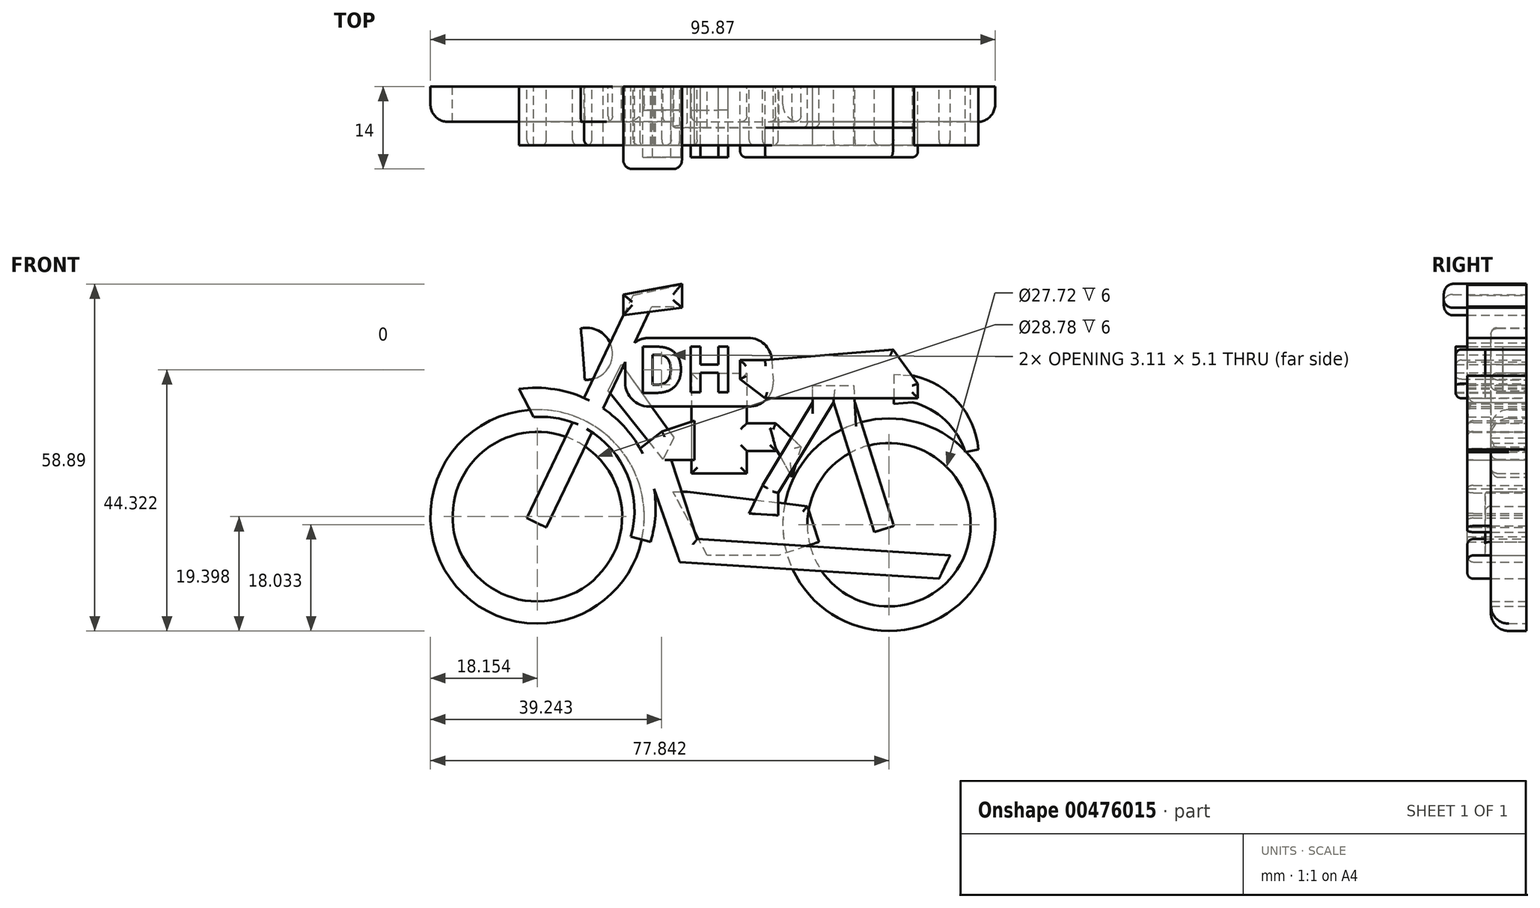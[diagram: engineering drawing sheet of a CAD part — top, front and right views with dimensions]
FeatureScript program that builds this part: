
annotation { "Feature Type Name" : "Feature", "Feature Type Description" : "" }
export const myFeature = defineFeature(function(context is Context, id is Id, definition is map)
    precondition{}
    {
        {
            var Q0;
            Q0=qCreatedBy(makeId("Front.planeOp"),FACE);
            var sketch = newSketch(context, id + "F0", { "sketchPlane" : qUnion([Q0])});
            skCircle(sketch, "E0", {"center": v(30.84, -8.07) * mm, "radius": 18.03 * mm});
            skCircle(sketch, "E1", {"center": v(30.84, -8.07) * mm, "radius": 13.86 * mm});
            skCircle(sketch, "E2", {"center": v(-28.85, -6.7) * mm, "radius": 18.15 * mm});
            skCircle(sketch, "E3", {"center": v(-28.85, -6.7) * mm, "radius": 14.4 * mm});
            skLineSegment(sketch, "E4.bottom", {"start": v(-2.69, 17.64) * mm, "end": v(6.7, 17.64) * mm});
            skLineSegment(sketch, "E4.top", {"start": v(-2.69, 0.65) * mm, "end": v(6.7, 0.65) * mm});
            skLineSegment(sketch, "E4.left", {"start": v(-2.69, 17.64) * mm, "end": v(-2.69, 0.65) * mm});
            skLineSegment(sketch, "E4.right", {"start": v(6.7, 17.64) * mm, "end": v(6.7, 0.65) * mm});
            skPoint(sketch, "E5.visualSharp", {"position": v(8.94, 22.1) * mm});
            skPoint(sketch, "E6.visualSharp", {"position": v(-12.3, 22.1) * mm});
            skPoint(sketch, "E7.visualSharp", {"position": v(-12.3, 13.62) * mm});
            skLineSegment(sketch, "E8.bottom", {"start": v(6.7, 9.14) * mm, "end": v(11.62, 9.14) * mm});
            skLineSegment(sketch, "E8.top", {"start": v(6.7, 9.14) * mm, "end": v(11.62, 9.14) * mm});
            skLineSegment(sketch, "E8.left", {"start": v(6.7, 9.14) * mm, "end": v(6.7, 9.14) * mm});
            skLineSegment(sketch, "E8.right", {"start": v(11.62, 9.14) * mm, "end": v(11.62, 9.14) * mm});
            skLineSegment(sketch, "E9.top", {"start": v(11.62, 4.45) * mm, "end": v(11.62, 4.45) * mm});
            skLineSegment(sketch, "E9.left", {"start": v(11.62, 9.14) * mm, "end": v(11.62, 4.45) * mm});
            skLineSegment(sketch, "E9.right", {"start": v(11.62, 9.14) * mm, "end": v(11.62, 4.45) * mm});
            skLineSegment(sketch, "E10.bottom", {"start": v(6.7, 4.9) * mm, "end": v(11.62, 4.9) * mm});
            skLineSegment(sketch, "E10.top", {"start": v(6.7, 4.45) * mm, "end": v(11.62, 4.45) * mm});
            skLineSegment(sketch, "E10.left", {"start": v(6.7, 4.9) * mm, "end": v(6.7, 4.45) * mm});
            skLineSegment(sketch, "E10.right", {"start": v(11.62, 4.9) * mm, "end": v(11.62, 4.45) * mm});
            skLineSegment(sketch, "E11", {"start": v(40.23, 12.05) * mm, "end": v(43.8, 15.4) * mm});
            skLineSegment(sketch, "E12", {"start": v(43.8, 15.4) * mm, "end": v(45.82, 9.14) * mm});
            skLineSegment(sketch, "E13", {"start": v(45.82, 9.14) * mm, "end": v(43.4, 8.37) * mm});
            skArc(sketch, "E14", {"start": v(-20.8, 16.52) * mm, "mid": v(-16.1, 21.27) * mm, "end": v(-21.46, 25.24) * mm});
            skLineSegment(sketch, "E15", {"start": v(-21.46, 25.24) * mm, "end": v(-20.8, 16.52) * mm});
            skLineSegment(sketch, "E16", {"start": v(11.62, 9.14) * mm, "end": v(15.89, 5.17) * mm});
            skLineSegment(sketch, "E17", {"start": v(15.89, 5.17) * mm, "end": v(14.4, 0) * mm});
            skLineSegment(sketch, "E18", {"start": v(14.4, 0) * mm, "end": v(11.62, 4.9) * mm});
            skLineSegment(sketch, "E19", {"start": v(-14.59, 19.16) * mm, "end": v(-5.65, 6.64) * mm});
            skLineSegment(sketch, "E20", {"start": v(-5.65, 6.64) * mm, "end": v(-7.52, 3.06) * mm});
            skLineSegment(sketch, "E21", {"start": v(-7.52, 3.06) * mm, "end": v(-16.82, 14.69) * mm});
            skLineSegment(sketch, "E22", {"start": v(-16.82, 14.69) * mm, "end": v(-14.59, 19.16) * mm});
            skSolve(sketch);
        }
        {
            var Q0;
            Q0=qCreatedBy(makeId("Front.planeOp"),FACE);
            var sketch = newSketch(context, id + "F1", { "sketchPlane" : qUnion([Q0])});
            skLineSegment(sketch, "E23", {"start": v(-12.62, 30.83) * mm, "end": v(-30.63, -6.95) * mm});
            skLineSegment(sketch, "E24", {"start": v(-30.63, -6.95) * mm, "end": v(-27.3, -8.54) * mm});
            skLineSegment(sketch, "E25", {"start": v(-27.3, -8.54) * mm, "end": v(-9.43, 28.94) * mm});
            skLineSegment(sketch, "E26", {"start": v(-9.43, 28.94) * mm, "end": v(-4.25, 28.94) * mm});
            skLineSegment(sketch, "E27", {"start": v(-4.25, 28.94) * mm, "end": v(-4.25, 32.61) * mm});
            skLineSegment(sketch, "E28", {"start": v(-4.25, 32.61) * mm, "end": v(-12.62, 30.83) * mm});
            skArc(sketch, "E29", {"start": v(-9.62, -10.97) * mm, "mid": v(-13.7, 8.11) * mm, "end": v(-31.97, 14.96) * mm});
            skArc(sketch, "E30", {"start": v(-12.97, -10.08) * mm, "mid": v(-15.96, 4.37) * mm, "end": v(-29.5, 10.2) * mm});
            skPoint(sketch, "E30.endSnap0", {"position": v(-18.36, 10.2) * mm});
            skLineSegment(sketch, "E31", {"start": v(-31.97, 14.96) * mm, "end": v(-29.5, 10.2) * mm});
            skLineSegment(sketch, "E32", {"start": v(-12.97, -10.08) * mm, "end": v(-9.62, -10.97) * mm});
            skArc(sketch, "E33", {"start": v(46.04, 4.67) * mm, "mid": v(42.6, 12.7) * mm, "end": v(35.09, 17.2) * mm});
            skArc(sketch, "E34", {"start": v(43.8, 4.23) * mm, "mid": v(40.43, 9.63) * mm, "end": v(34.87, 12.72) * mm});
            skLineSegment(sketch, "E35", {"start": v(35.09, 17.2) * mm, "end": v(34.87, 12.72) * mm});
            skLineSegment(sketch, "E36", {"start": v(43.8, 4.23) * mm, "end": v(46.04, 4.67) * mm});
            skLineSegment(sketch, "E37", {"start": v(25.03, 12.72) * mm, "end": v(31.64, -8.3) * mm});
            skLineSegment(sketch, "E38", {"start": v(31.64, -8.3) * mm, "end": v(28.36, -9.32) * mm});
            skLineSegment(sketch, "E39", {"start": v(28.36, -9.32) * mm, "end": v(21.42, 12.72) * mm});
            skLineSegment(sketch, "E40", {"start": v(21.42, 12.72) * mm, "end": v(25.03, 12.72) * mm});
            skLineSegment(sketch, "E41", {"start": v(17.88, 12.72) * mm, "end": v(21.42, 12.72) * mm});
            skLineSegment(sketch, "E42", {"start": v(12.07, -2.7) * mm, "end": v(9.35, -1.4) * mm});
            skLineSegment(sketch, "E43", {"start": v(9.35, -1.4) * mm, "end": v(17.88, 12.72) * mm});
            skLineSegment(sketch, "E44", {"start": v(12.07, -2.7) * mm, "end": v(21.42, 12.72) * mm});
            skLineSegment(sketch, "E45", {"start": v(-4.67, -14.4) * mm, "end": v(39.34, -17.23) * mm});
            skLineSegment(sketch, "E46", {"start": v(39.34, -17.23) * mm, "end": v(41.22, -13.28) * mm});
            skLineSegment(sketch, "E47", {"start": v(41.22, -13.28) * mm, "end": v(-1.72, -10.5) * mm});
            skLineSegment(sketch, "E48", {"start": v(-7.71, 7.77) * mm, "end": v(-2.17, 9.59) * mm});
            skLineSegment(sketch, "E49", {"start": v(-2.17, 9.59) * mm, "end": v(-2.17, 2.89) * mm});
            skLineSegment(sketch, "E50", {"start": v(-2.17, 2.89) * mm, "end": v(-6.11, 2.89) * mm});
            skLineSegment(sketch, "E51", {"start": v(9.35, -1.4) * mm, "end": v(7.08, -6.16) * mm});
            skLineSegment(sketch, "E52", {"start": v(7.08, -6.16) * mm, "end": v(9.35, -6.3) * mm});
            skLineSegment(sketch, "E53", {"start": v(9.35, -6.3) * mm, "end": v(12.07, -6.48) * mm});
            skLineSegment(sketch, "E54", {"start": v(12.07, -6.48) * mm, "end": v(12.07, -2.7) * mm});
            skLineSegment(sketch, "E55", {"start": v(35.09, 17.2) * mm, "end": v(31.64, 17.36) * mm});
            skLineSegment(sketch, "E56", {"start": v(31.64, 17.36) * mm, "end": v(31.64, 12.47) * mm});
            skLineSegment(sketch, "E57", {"start": v(31.64, 12.47) * mm, "end": v(34.87, 12.72) * mm});
            skLineSegment(sketch, "E58", {"start": v(-7.71, 7.77) * mm, "end": v(-11.42, 4.88) * mm});
            skLineSegment(sketch, "E59", {"start": v(-11.42, 4.88) * mm, "end": v(-4.67, -14.4) * mm});
            skLineSegment(sketch, "E60", {"start": v(-1.72, -10.5) * mm, "end": v(-6.11, 2.89) * mm});
            skLineSegment(sketch, "E61", {"start": v(17.88, 12.72) * mm, "end": v(17.88, 15.58) * mm});
            skLineSegment(sketch, "E62", {"start": v(17.88, 15.58) * mm, "end": v(24.87, 15.58) * mm});
            skLineSegment(sketch, "E63", {"start": v(24.87, 15.58) * mm, "end": v(25.03, 12.72) * mm});
            skLineSegment(sketch, "E64", {"start": v(7.2, 12) * mm, "end": v(-9.92, 12) * mm});
            skLineSegment(sketch, "E65", {"start": v(-13.92, 16) * mm, "end": v(-13.92, 19.63) * mm});
            skLineSegment(sketch, "E66", {"start": v(-9.92, 23.63) * mm, "end": v(6.97, 23.63) * mm});
            skLineSegment(sketch, "E67", {"start": v(10.96, 19.88) * mm, "end": v(11.19, 16.25) * mm});
            skPoint(sketch, "E68.visualSharp", {"position": v(10.73, 23.63) * mm});
            skArc(sketch, "E68.filletArc", {"start": v(10.96, 19.88) * mm, "mid": v(9.7, 22.54) * mm, "end": v(6.97, 23.63) * mm});
            skPoint(sketch, "E69.visualSharp", {"position": v(-13.92, 23.63) * mm});
            skArc(sketch, "E69.filletArc", {"start": v(-9.92, 23.63) * mm, "mid": v(-12.74, 22.46) * mm, "end": v(-13.92, 19.63) * mm});
            skPoint(sketch, "E70.visualSharp", {"position": v(-13.92, 12) * mm});
            skArc(sketch, "E70.filletArc", {"start": v(-13.92, 16) * mm, "mid": v(-12.74, 13.18) * mm, "end": v(-9.92, 12) * mm});
            skPoint(sketch, "E71.visualSharp", {"position": v(11.45, 12) * mm});
            skArc(sketch, "E71.filletArc", {"start": v(7.2, 12) * mm, "mid": v(10.11, 13.27) * mm, "end": v(11.19, 16.25) * mm});
            skSolve(sketch);
        }
        {
            var Q0;
            Q0=qCreatedBy(makeId("Front.planeOp"),FACE);
            var sketch = newSketch(context, id + "F2", { "sketchPlane" : qUnion([Q0])});
            skLineSegment(sketch, "E72", {"start": v(-3.36, -2.48) * mm, "end": v(16.98, -4.94) * mm});
            skLineSegment(sketch, "E73", {"start": v(16.98, -4.94) * mm, "end": v(19, -10.97) * mm});
            skLineSegment(sketch, "E74", {"start": v(19, -10.97) * mm, "end": v(12.16, -13.25) * mm});
            skLineSegment(sketch, "E75", {"start": v(12.16, -13.25) * mm, "end": v(0, -13.25) * mm});
            skLineSegment(sketch, "E76", {"start": v(0, -13.25) * mm, "end": v(-5.82, -2.48) * mm});
            skLineSegment(sketch, "E77", {"start": v(-5.82, -2.48) * mm, "end": v(-3.36, -2.48) * mm});
            skLineSegment(sketch, "E78", {"start": v(9.83, 19.87) * mm, "end": v(9.83, 13.4) * mm});
            skLineSegment(sketch, "E79", {"start": v(9.83, 13.4) * mm, "end": v(19, 13.4) * mm});
            skLineSegment(sketch, "E80", {"start": v(19, 13.4) * mm, "end": v(35.76, 13.4) * mm});
            skLineSegment(sketch, "E81", {"start": v(35.76, 13.4) * mm, "end": v(35.76, 15.85) * mm});
            skLineSegment(sketch, "E82", {"start": v(35.76, 15.85) * mm, "end": v(31.51, 21.66) * mm});
            skLineSegment(sketch, "E83", {"start": v(31.51, 21.66) * mm, "end": v(9.83, 19.87) * mm});
            skLineSegment(sketch, "E84", {"start": v(5.58, 19.87) * mm, "end": v(5.58, 16.63) * mm});
            skPoint(sketch, "E84.endSnap0", {"position": v(9.83, 16.63) * mm});
            skLineSegment(sketch, "E85", {"start": v(5.58, 16.63) * mm, "end": v(9.83, 13.4) * mm});
            skLineSegment(sketch, "E86", {"start": v(9.83, 19.87) * mm, "end": v(5.58, 19.87) * mm});
            skSolve(sketch);
        }
        {
            var Q0;
            Q0=qCreatedBy(makeId("Front.planeOp"),FACE);
            var sketch = newSketch(context, id + "F3", { "sketchPlane" : qUnion([Q0])});
            skLineSegment(sketch, "E87", {"start": v(-14.25, 27.47) * mm, "end": v(-14.25, 31) * mm});
            skPoint(sketch, "E88.secondSnap0", {"position": v(-33.62, -11.67) * mm});
            skLineSegment(sketch, "E89", {"start": v(-4.3, 32.8) * mm, "end": v(-14.25, 31) * mm});
            skLineSegment(sketch, "E90", {"start": v(-4.3, 32.8) * mm, "end": v(-4.3, 28.75) * mm});
            skLineSegment(sketch, "E91", {"start": v(-4.3, 28.75) * mm, "end": v(-14.25, 27.47) * mm});
            skSolve(sketch);
        }
        {
            var Q0;
            Q0 = qSketchRegion(id + "F0", true);
            extrude(context, id + "F4", {"entities" : qUnion([Q0]), "depth" : 6 * mm});
        }
        {
            var Q0;
            Q0 = qSketchRegion(id + "F1", true);
            extrude(context, id + "F5", {"entities" : qUnion([Q0]), "depth" : 10 * mm});
        }
        {
            var Q0;
            Q0 = qSketchRegion(id + "F2", true);
            extrude(context, id + "F6", {"entities" : qUnion([Q0]), "depth" : 7 * mm});
        }
        {
            var Q0;
            Q0 = qSketchRegion(id + "F3", true);
            extrude(context, id + "F7", {"entities" : qUnion([Q0]), "depth" : 14 * mm});
        }
        {
            var Q0;
            Q0=makeQuery(id+"F6.opExtrude","CAP_FACE",FACE,{"disambiguationData":[OSD([sQuery(id+"F2.wireOp",EDGE,"E79"),sQuery(id+"F2.wireOp",EDGE,"E80"),sQuery(id+"F2.wireOp",EDGE,"E81"),sQuery(id+"F2.wireOp",EDGE,"E82"),sQuery(id+"F2.wireOp",EDGE,"E83"),sQuery(id+"F2.wireOp",EDGE,"E84"),sQuery(id+"F2.wireOp",EDGE,"E85"),sQuery(id+"F2.wireOp",EDGE,"E86")])],"isStart":false});
            extrude(context, id + "F8", {"entities" : qUnion([Q0]), "depth" : 5 * mm});
        }
        {
            var Q0;
            Q0=makeQuery(id+"F4.opExtrude","CAP_EDGE",EDGE,{"disambiguationData":[OSD([sQuery(id+"F0.wireOp",EDGE,"E0")])],"isStart":false});
            fillet(context, id + "F9", {"entities" : qUnion([Q0]), "radius" : 3 * mm, "tangentPropagation" : true, "allowEdgeOverflow" : false});
        }
        {
            var Q0;
            Q0=makeQuery(id+"F4.opExtrude","CAP_EDGE",EDGE,{"disambiguationData":[OSD([sQuery(id+"F0.wireOp",EDGE,"E2")])],"isStart":false});
            fillet(context, id + "F10", {"entities" : qUnion([Q0]), "radius" : 3 * mm, "tangentPropagation" : true, "allowEdgeOverflow" : false});
        }
        {
            var Q0;
            Q0=makeQuery(id+"F5.opExtrude","CAP_EDGE",EDGE,{"disambiguationData":[OSD([sQuery(id+"F1.wireOp",EDGE,"E37")])],"isStart":false});
            var Q1;
            Q1=makeQuery(id+"F5.opExtrude","CAP_EDGE",EDGE,{"disambiguationData":[OSD([sQuery(id+"F1.wireOp",EDGE,"E39")])],"isStart":false});
            var Q2;
            Q2=makeQuery(id+"F5.opExtrude","CAP_EDGE",EDGE,{"disambiguationData":[OSD([sQuery(id+"F1.wireOp",EDGE,"E44")])],"isStart":false});
            var Q3;
            Q3=makeQuery(id+"F5.opExtrude","CAP_EDGE",EDGE,{"disambiguationData":[OSD([sQuery(id+"F1.wireOp",EDGE,"E43")])],"isStart":false});
            var Q4;
            Q4=makeQuery(id+"F5.opExtrude","CAP_EDGE",EDGE,{"disambiguationData":[OSD([sQuery(id+"F1.wireOp",EDGE,"E51")])],"isStart":false});
            var Q5;
            Q5=makeQuery(id+"F5.opExtrude","CAP_EDGE",EDGE,{"disambiguationData":[OSD([sQuery(id+"F1.wireOp",EDGE,"E54")])],"isStart":false});
            var Q6;
            Q6=makeQuery(id+"F6.opExtrude","CAP_EDGE",EDGE,{"disambiguationData":[OSD([sQuery(id+"F2.wireOp",EDGE,"E72")])],"isStart":false});
            var Q7;
            Q7=makeQuery(id+"F6.opExtrude","CAP_EDGE",EDGE,{"disambiguationData":[OSD([sQuery(id+"F2.wireOp",EDGE,"E73")])],"isStart":false});
            var Q8;
            Q8=makeQuery(id+"F5.opExtrude","CAP_EDGE",EDGE,{"disambiguationData":[OSD([sQuery(id+"F1.wireOp",EDGE,"E47")])],"isStart":false});
            var Q9;
            Q9=makeQuery(id+"F5.opExtrude","CAP_EDGE",EDGE,{"disambiguationData":[OSD([sQuery(id+"F1.wireOp",EDGE,"E45")])],"isStart":false});
            var Q10;
            Q10=makeQuery(id+"F8.opExtrude","CAP_EDGE",EDGE,{"disambiguationData":[OSD([sQuery(id+"F2.wireOp",EDGE,"E83")])],"isStart":false});
            var Q11;
            Q11=makeQuery(id+"F8.opExtrude","CAP_EDGE",EDGE,{"disambiguationData":[OSD([sQuery(id+"F2.wireOp",EDGE,"E82")])],"isStart":false});
            var Q12;
            Q12=makeQuery(id+"F8.opExtrude","CAP_EDGE",EDGE,{"disambiguationData":[OSD([sQuery(id+"F2.wireOp",EDGE,"E81")])],"isStart":false});
            var Q13;
            Q13=makeQuery(id+"F8.opExtrude","CAP_FACE",FACE,{"disambiguationData":[OSD([sQuery(id+"F2.wireOp",EDGE,"E79"),sQuery(id+"F2.wireOp",EDGE,"E80"),sQuery(id+"F2.wireOp",EDGE,"E81"),sQuery(id+"F2.wireOp",EDGE,"E82"),sQuery(id+"F2.wireOp",EDGE,"E83"),sQuery(id+"F2.wireOp",EDGE,"E84"),sQuery(id+"F2.wireOp",EDGE,"E85"),sQuery(id+"F2.wireOp",EDGE,"E86")])],"isStart":false});
            fillet(context, id + "F11", {"entities" : qUnion([Q0, Q1, Q2, Q3, Q4, Q5, Q6, Q7, Q8, Q9, Q10, Q11, Q12, Q13]), "radius" : 1 * mm, "tangentPropagation" : true, "allowEdgeOverflow" : false});
        }
        {
            var Q0;
            Q0=makeQuery(id+"F4.opExtrude","CAP_FACE",FACE,{"disambiguationData":[OSD([sQuery(id+"F0.wireOp",EDGE,"E4.bottom"),sQuery(id+"F0.wireOp",EDGE,"E4.top"),sQuery(id+"F0.wireOp",EDGE,"E4.left"),sQuery(id+"F0.wireOp",EDGE,"E4.right"),sQuery(id+"F0.wireOp",EDGE,"E8.top"),sQuery(id+"F0.wireOp",EDGE,"E10.top"),sQuery(id+"F0.wireOp",EDGE,"E10.right"),sQuery(id+"F0.wireOp",EDGE,"E16"),sQuery(id+"F0.wireOp",EDGE,"E17"),sQuery(id+"F0.wireOp",EDGE,"E18")])],"isStart":false});
            fillet(context, id + "F12", {"entities" : qUnion([Q0]), "radius" : 1 * mm, "tangentPropagation" : true, "allowEdgeOverflow" : false});
        }
        {
            var Q0;
            Q0=makeQuery(id+"F7.opExtrude","CAP_FACE",FACE,{"disambiguationData":[OSD([sQuery(id+"F3.wireOp",EDGE,"E87"),sQuery(id+"F3.wireOp",EDGE,"E89"),sQuery(id+"F3.wireOp",EDGE,"E90"),sQuery(id+"F3.wireOp",EDGE,"E91")])],"isStart":false});
            fillet(context, id + "F13", {"entities" : qUnion([Q0]), "radius" : 1.5 * mm, "tangentPropagation" : true, "allowEdgeOverflow" : false});
        }
        {
            var Q0;
            Q0=makeQuery(id+"F4.opExtrude","CAP_EDGE",EDGE,{"disambiguationData":[OSD([sQuery(id+"F0.wireOp",EDGE,"E21")])],"isStart":false});
            var Q1;
            Q1=makeQuery(id+"F5.opExtrude","CAP_EDGE",EDGE,{"disambiguationData":[OSD([sQuery(id+"F1.wireOp",EDGE,"E60")])],"isStart":false});
            var Q2;
            Q2=makeQuery(id+"F5.opExtrude","CAP_EDGE",EDGE,{"disambiguationData":[OSD([sQuery(id+"F1.wireOp",EDGE,"E58")])],"isStart":false});
            var Q3;
            Q3=makeQuery(id+"F5.opExtrude","CAP_EDGE",EDGE,{"disambiguationData":[OSD([sQuery(id+"F1.wireOp",EDGE,"E48")])],"isStart":false});
            var Q4;
            {var subQ0=sQuery(id+"F1.wireOp",EDGE,"E25");Q4=makeQuery(id+"F5.opExtrude","CAP_EDGE",EDGE,{"disambiguationData":[OSD([subQ0]),TDD([makeQuery(id+"F1.imprint","IMPRINT",EDGE,{"disambiguationData":[TD([[makeQuery(id+"F1.imprint","INTERSECT",VERTEX,{"derivedFrom":[sQuery(id+"F1.wireOp",EDGE,"E24"),subQ0]}),-1.0]])],"derivedFrom":subQ0})])],"isStart":false});}
            var Q5;
            {var subQ0=sQuery(id+"F1.wireOp",EDGE,"E23");Q5=makeQuery(id+"F5.opExtrude","CAP_EDGE",EDGE,{"disambiguationData":[OSD([subQ0]),TDD([makeQuery(id+"F1.imprint","IMPRINT",EDGE,{"disambiguationData":[TD([[makeQuery(id+"F1.imprint","INTERSECT",VERTEX,{"derivedFrom":[subQ0,sQuery(id+"F1.wireOp",EDGE,"E24")]}),1.0]])],"derivedFrom":subQ0})])],"isStart":false});}
            var Q6;
            {var subQ0=sQuery(id+"F1.wireOp",EDGE,"E23");Q6=makeQuery(id+"F5.opExtrude","CAP_EDGE",EDGE,{"disambiguationData":[OSD([subQ0]),TDD([makeQuery(id+"F1.imprint","IMPRINT",EDGE,{"disambiguationData":[TD([[makeQuery(id+"F1.imprint","INTERSECT",VERTEX,{"derivedFrom":[subQ0,sQuery(id+"F1.wireOp",EDGE,"E28")]}),-1.0]])],"derivedFrom":subQ0})])],"isStart":false});}
            var Q7;
            Q7=makeQuery(id+"F4.opExtrude","CAP_EDGE",EDGE,{"disambiguationData":[OSD([sQuery(id+"F0.wireOp",EDGE,"E14")])],"isStart":false});
            fillet(context, id + "F14", {"entities" : qUnion([Q0, Q1, Q2, Q3, Q4, Q5, Q6, Q7]), "radius" : 1 * mm, "tangentPropagation" : true, "allowEdgeOverflow" : false});
        }
        {
            var Q0;
            Q0=qCreatedBy(makeId("Front.planeOp"),FACE);
            var sketch = newSketch(context, id + "F15", { "sketchPlane" : qUnion([Q0])});
            skPoint(sketch, "E92.secondSnap0", {"position": v(-2.73, 17.22) * mm});
            skText(sketch, "E93", { "text": "D", "fontName": "OpenSans-Bold.ttf"});
            skText(sketch, "E94", { "text": "H", "fontName": "OpenSans-Bold.ttf"});
            const initialGuessF15  = {"E93": [-0.01196, 0.0143, 1, 0, 0.0079], "E94": [-0.00377, 0.0144, 1, 0, 0.00779]};
            skSetInitialGuess(sketch, initialGuessF15);
            skSolve(sketch);
        }
        {
            var Q0;
            Q0 = qSketchRegion(id + "F15", true);
            extrude(context, id + "F16", {"entities" : qUnion([Q0]), "depth" : 4 * mm});
        }
        {
            var Q0;
            Q0 = qSketchRegion(id + "F15", true);
            extrude(context, id + "F17", {"entities" : qUnion([Q0]), "depth" : 12 * mm});
        }
    });
